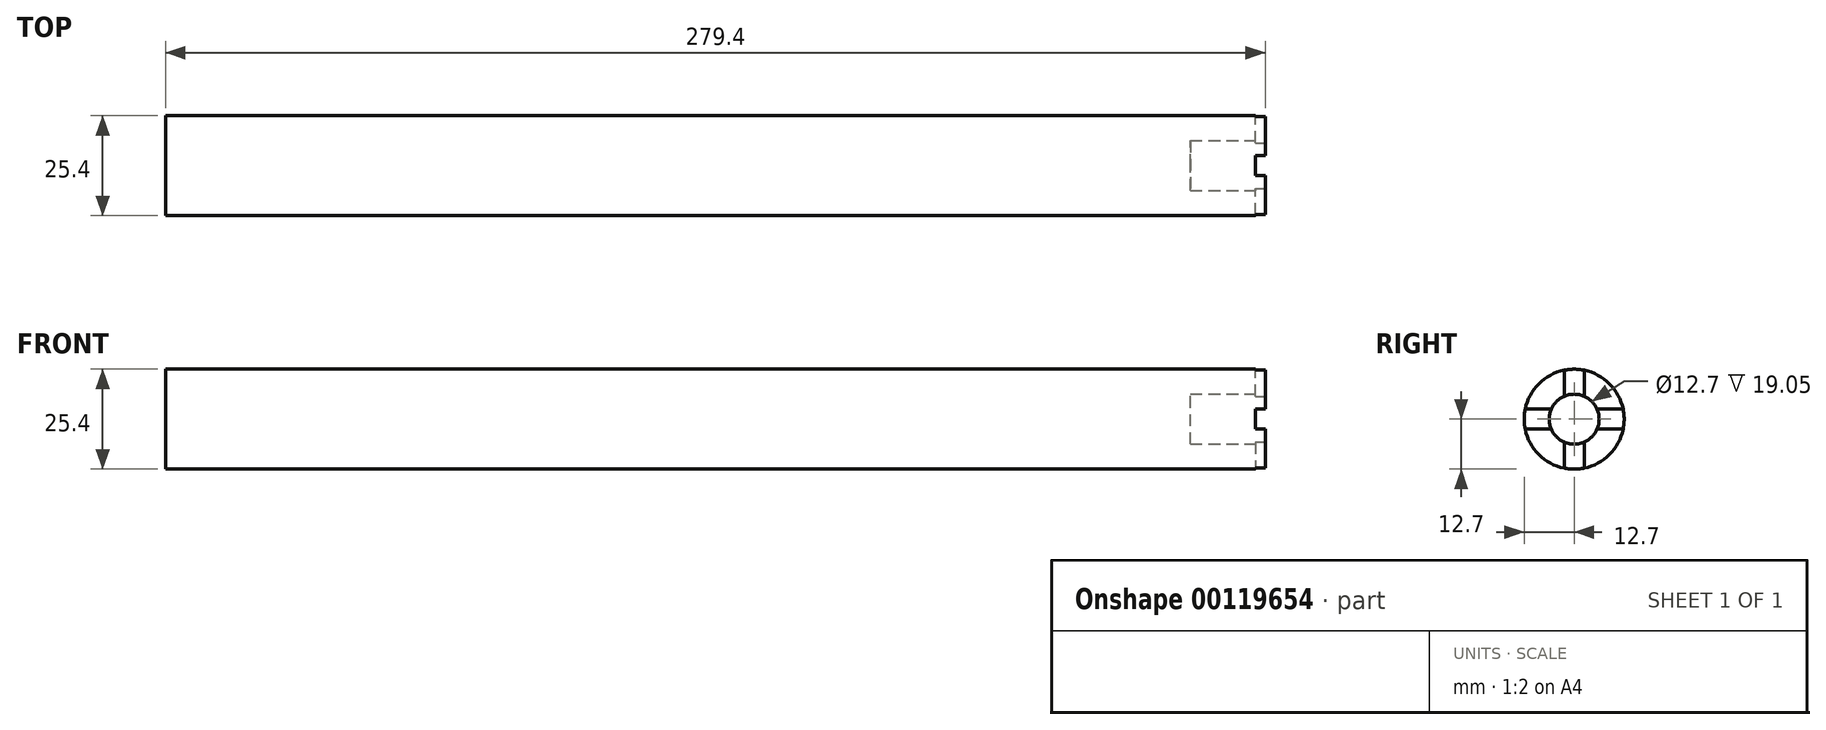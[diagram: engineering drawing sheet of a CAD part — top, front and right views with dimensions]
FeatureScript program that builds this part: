
annotation { "Feature Type Name" : "Feature", "Feature Type Description" : "" }
export const myFeature = defineFeature(function(context is Context, id is Id, definition is map)
    precondition{}
    {
        {
            var Q0;
            Q0=qCreatedBy(makeId("Right.planeOp"),FACE);
            var sketch = newSketch(context, id + "F0", { "sketchPlane" : qUnion([Q0])});
            skCircle(sketch, "E0", {"center": v(0, 0) * mm, "radius": 12.7 * mm});
            skSolve(sketch);
        }
        {
            var Q0;
            Q0 = qSketchRegion(id + "F0", true);
            extrude(context, id + "F1", {"entities" : qUnion([Q0]), "oppositeDirection" : true, "depth" : 279.4 * mm});
        }
        {
            var Q0;
            Q0=qCreatedBy(makeId("Right.planeOp"),FACE);
            var sketch = newSketch(context, id + "F2", { "sketchPlane" : qUnion([Q0])});
            skCircle(sketch, "E1", {"center": v(0, 0) * mm, "radius": 6.35 * mm});
            skLineSegment(sketch, "E2", {"start": v(-2.54, 5.82) * mm, "end": v(-2.54, 13.44) * mm});
            skLineSegment(sketch, "E3", {"start": v(2.54, 13.44) * mm, "end": v(2.54, 5.82) * mm});
            skLineSegment(sketch, "E4", {"start": v(0, 0) * mm, "end": v(0, 19.1) * mm, "construction": true});
            skLineSegment(sketch, "E5", {"start": v(-2.54, 13.44) * mm, "end": v(2.54, 13.44) * mm});
            skLineSegment(sketch, "E6", {"start": v(-2.54, 5.82) * mm, "end": v(2.54, 5.82) * mm});
            skLineSegment(sketch, "E7.bottom", {"start": v(5.82, -2.54) * mm, "end": v(13.44, -2.54) * mm});
            skLineSegment(sketch, "E7.top", {"start": v(5.82, 2.54) * mm, "end": v(13.44, 2.54) * mm});
            skLineSegment(sketch, "E7.left", {"start": v(5.82, -2.54) * mm, "end": v(5.82, 2.54) * mm});
            skLineSegment(sketch, "E7.right", {"start": v(13.44, -2.54) * mm, "end": v(13.44, 2.54) * mm});
            skLineSegment(sketch, "E8.bottom", {"start": v(-13.44, -2.54) * mm, "end": v(-5.82, -2.54) * mm});
            skLineSegment(sketch, "E8.top", {"start": v(-13.44, 2.54) * mm, "end": v(-5.82, 2.54) * mm});
            skLineSegment(sketch, "E8.left", {"start": v(-13.44, -2.54) * mm, "end": v(-13.44, 2.54) * mm});
            skLineSegment(sketch, "E8.right", {"start": v(-5.82, -2.54) * mm, "end": v(-5.82, 2.54) * mm});
            skLineSegment(sketch, "E9.bottom", {"start": v(-2.54, -5.82) * mm, "end": v(2.54, -5.82) * mm});
            skLineSegment(sketch, "E9.top", {"start": v(-2.54, -13.44) * mm, "end": v(2.54, -13.44) * mm});
            skLineSegment(sketch, "E9.left", {"start": v(-2.54, -5.82) * mm, "end": v(-2.54, -13.44) * mm});
            skLineSegment(sketch, "E9.right", {"start": v(2.54, -5.82) * mm, "end": v(2.54, -13.44) * mm});
            skSolve(sketch);
        }
        {
            var Q0;
            {var subQ1=sQuery(id+"F2.wireOp",EDGE,"E2");Q0=makeQuery(id+"F2.imprint","IMPRINT",FACE,{"disambiguationData":[TD([[makeQuery(id+"F2.imprint","IMPRINT",EDGE,{"derivedFrom":subQ1}),-1.0]])]});}
            var Q1;
            {var subQ1=sQuery(id+"F2.wireOp",EDGE,"E8.bottom");Q1=makeQuery(id+"F2.imprint","IMPRINT",FACE,{"disambiguationData":[TD([[makeQuery(id+"F2.imprint","IMPRINT",EDGE,{"derivedFrom":subQ1}),1.0]])]});}
            var Q2;
            Q2=makeQuery(id+"F2.imprint","IMPRINT",FACE,{"disambiguationData":[TD([[makeQuery(id+"F2.imprint","IMPRINT",EDGE,{"derivedFrom":sQuery(id+"F2.wireOp",EDGE,"E9.top")}),1.0]])]});
            var Q3;
            {var subQ1=sQuery(id+"F2.wireOp",EDGE,"E7.bottom");Q3=makeQuery(id+"F2.imprint","IMPRINT",FACE,{"disambiguationData":[TD([[makeQuery(id+"F2.imprint","IMPRINT",EDGE,{"derivedFrom":subQ1}),1.0]])]});}
            extrude(context, id + "F3", {"entities" : qUnion([Q0, Q1, Q2, Q3]), "operationType" : NewBodyOperationType.REMOVE, "oppositeDirection" : true, "depth" : 2.54 * mm});
        }
        {
            var Q0;
            {var subQ4=sQuery(id+"F2.wireOp",EDGE,"E6");Q0=makeQuery(id+"F2.imprint","IMPRINT",FACE,{"disambiguationData":[TD([[makeQuery(id+"F2.imprint","IMPRINT",EDGE,{"derivedFrom":subQ4}),-1.0]])]});}
            var Q1;
            {var subQ0=sQuery(id+"F2.wireOp",EDGE,"E6");Q1=makeQuery(id+"F2.imprint","IMPRINT",FACE,{"disambiguationData":[TD([[makeQuery(id+"F2.imprint","IMPRINT",EDGE,{"derivedFrom":subQ0}),1.0]])]});}
            var Q2;
            {var subQ0=sQuery(id+"F2.wireOp",EDGE,"E8.right");Q2=makeQuery(id+"F2.imprint","IMPRINT",FACE,{"disambiguationData":[TD([[makeQuery(id+"F2.imprint","IMPRINT",EDGE,{"derivedFrom":subQ0}),1.0]])]});}
            var Q3;
            {var subQ0=sQuery(id+"F2.wireOp",EDGE,"E9.bottom");Q3=makeQuery(id+"F2.imprint","IMPRINT",FACE,{"disambiguationData":[TD([[makeQuery(id+"F2.imprint","IMPRINT",EDGE,{"derivedFrom":subQ0}),-1.0]])]});}
            var Q4;
            {var subQ0=sQuery(id+"F2.wireOp",EDGE,"E7.left");Q4=makeQuery(id+"F2.imprint","IMPRINT",FACE,{"disambiguationData":[TD([[makeQuery(id+"F2.imprint","IMPRINT",EDGE,{"derivedFrom":subQ0}),-1.0]])]});}
            extrude(context, id + "F4", {"entities" : qUnion([Q0, Q1, Q2, Q3, Q4]), "operationType" : NewBodyOperationType.REMOVE, "oppositeDirection" : true, "depth" : 19.05 * mm});
        }
    });
